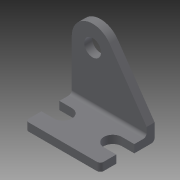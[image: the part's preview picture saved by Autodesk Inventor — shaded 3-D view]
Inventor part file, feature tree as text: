
AUTODESK INVENTOR PART (.ipt)
format: ipt  version: 2014 (Build 180170000, 170)  size: 183,296 bytes
history: native  units: in
note: dims shown in document units (in); Inventor stores cm internally (conversion verified against a paired STEP export)
features: other x147, sketch x8, extrude x5, hole x3
ambient origin geometry x8: Origin, YZ Plane, XZ Plane, XY Plane, X Axis, Y Axis, Z Axis, Center Point
bodies: Solid1 (feature_tree)
feature tree (163):
  extrude  "Extrusion1"  Depth=0.817in TaperAngle=0.0deg
  extrude  "Extrusion2"  Depth=0.1196in TaperAngle=0.0deg
  hole  "Hole1"  [1 undecoded]
  hole  "Hole2"  [1 undecoded]
  hole  "Hole3"  [1 undecoded]
  sketch  "Sketch_6"
  sketch  "Sketch_7"
  extrude  "Extrusion3"  [1 undecoded]
  extrude  "Extrusion4"  [1 undecoded]
  extrude  "Extrusion5"  [1 undecoded]
  other  "a1_XY"
  other  "a1_YZ"
  other  "a1_ZX"
  other  "a1_X"
  other  "a1_Y"
  other  "a1_Z"
  other  "a1_Center"
  other  "a2_XY"
  other  "a2_YZ"
  other  "a2_ZX"
  other  "a2_X"
  other  "a2_Y"
  other  "a2_Z"
  other  "a2_Center"
  other  "b1_XY"
  other  "b1_YZ"
  other  "b1_ZX"
  other  "b1_X"
  other  "b1_Y"
  other  "b1_Z"
  other  "b1_Center"
  other  "b2_XY"
  other  "b2_YZ"
  other  "b2_ZX"
  other  "b2_X"
  other  "b2_Y"
  other  "b2_Z"
  other  "b2_Center"
  other  "d1_XY"
  other  "d1_YZ"
  other  "d1_ZX"
  other  "d1_X"
  other  "d1_Y"
  other  "d1_Z"
  other  "d1_Center"
  other  "d2_XY"
  other  "d2_YZ"
  other  "d2_ZX"
  other  "d2_X"
  other  "d2_Y"
  other  "d2_Z"
  other  "d2_Center"
  other  "e1_XY"
  other  "e1_YZ"
  other  "e1_ZX"
  other  "e1_X"
  other  "e1_Y"
  other  "e1_Z"
  other  "e1_Center"
  other  "e2_XY"
  other  "e2_YZ"
  other  "e2_ZX"
  other  "e2_X"
  other  "e2_Y"
  other  "e2_Z"
  other  "e2_Center"
  other  "f1_XY"
  other  "f1_YZ"
  other  "f1_ZX"
  other  "f1_X"
  other  "f1_Y"
  other  "f1_Z"
  other  "f1_Center"
  other  "f2_XY"
  other  "f2_YZ"
  other  "f2_ZX"
  other  "f2_X"
  other  "f2_Y"
  other  "f2_Z"
  other  "f2_Center"
  other  "g1_XY"
  other  "g1_YZ"
  other  "g1_ZX"
  other  "g1_X"
  other  "g1_Y"
  other  "g1_Z"
  other  "g1_Center"
  other  "g2_XY"
  other  "g2_YZ"
  other  "g2_ZX"
  other  "g2_X"
  other  "g2_Y"
  other  "g2_Z"
  other  "g2_Center"
  other  "h1_XY"
  other  "h1_YZ"
  other  "h1_ZX"
  other  "h1_X"
  other  "h1_Y"
  other  "h1_Z"
  other  "h1_Center"
  other  "h2_XY"
  other  "h2_YZ"
  other  "h2_ZX"
  other  "h2_X"
  other  "h2_Y"
  other  "h2_Z"
  other  "h2_Center"
  other  "i_XY"
  other  "i_YZ"
  other  "i_ZX"
  other  "i_X"
  other  "i_Y"
  other  "i_Z"
  other  "i_Center"
  other  "j1_XY"
  other  "j1_YZ"
  other  "j1_ZX"
  other  "j1_X"
  other  "j1_Y"
  other  "j1_Z"
  other  "j1_Center"
  other  "j2_XY"
  other  "j2_YZ"
  other  "j2_ZX"
  other  "j2_X"
  other  "j2_Y"
  other  "j2_Z"
  other  "j2_Center"
  other  "k11_XY"
  other  "k11_YZ"
  other  "k11_ZX"
  other  "k11_X"
  other  "k11_Y"
  other  "k11_Z"
  other  "k11_Center"
  other  "k12_XY"
  other  "k12_YZ"
  other  "k12_ZX"
  other  "k12_X"
  other  "k12_Y"
  other  "k12_Z"
  other  "k12_Center"
  other  "to_dummy_L_XY"
  other  "to_dummy_L_YZ"
  other  "to_dummy_L_ZX"
  other  "to_dummy_L_X"
  other  "to_dummy_L_Y"
  other  "to_dummy_L_Z"
  other  "to_dummy_L_Center"
  other  "to_pin_L_XY"
  other  "to_pin_L_YZ"
  other  "to_pin_L_ZX"
  other  "to_pin_L_X"
  other  "to_pin_L_Y"
  other  "to_pin_L_Z"
  other  "to_pin_L_Center"
  sketch  "Sketch_1"  dims[d0=1.125in d1=0.0in d2=0.817in d3=0.0in]
  sketch  "Sketch_2"  dims[d4=0.2528in d5=0.75in d6=0.375in d7=0.25in d8=0.5635in d9=0.1196in d10=0.0in]
  sketch  "Sketch3"  dims[d11=0.27in d12=0.75in d13=0.375in d14=0.25in d15=0.5635in d16=0.1196in d17=0.0in]
  sketch  "Sketch4"  dims[d18=0.27in d19=0.75in d20=0.375in d21=0.25in d22=0.5635in d23=0.1196in d24=0.0in d25=0.1196in d26=0.0in]
  sketch  "Sketch5"  dims[d27=0.1196in d28=0.0in d29=0.1196in d30=0.0in]
  sketch  "Sketch_8"
note: 6 required parameter values undecoded (feature->parameter linkage not recoverable at this tier; creation-order binding heuristic only, values carry confidence <= 0.55)
